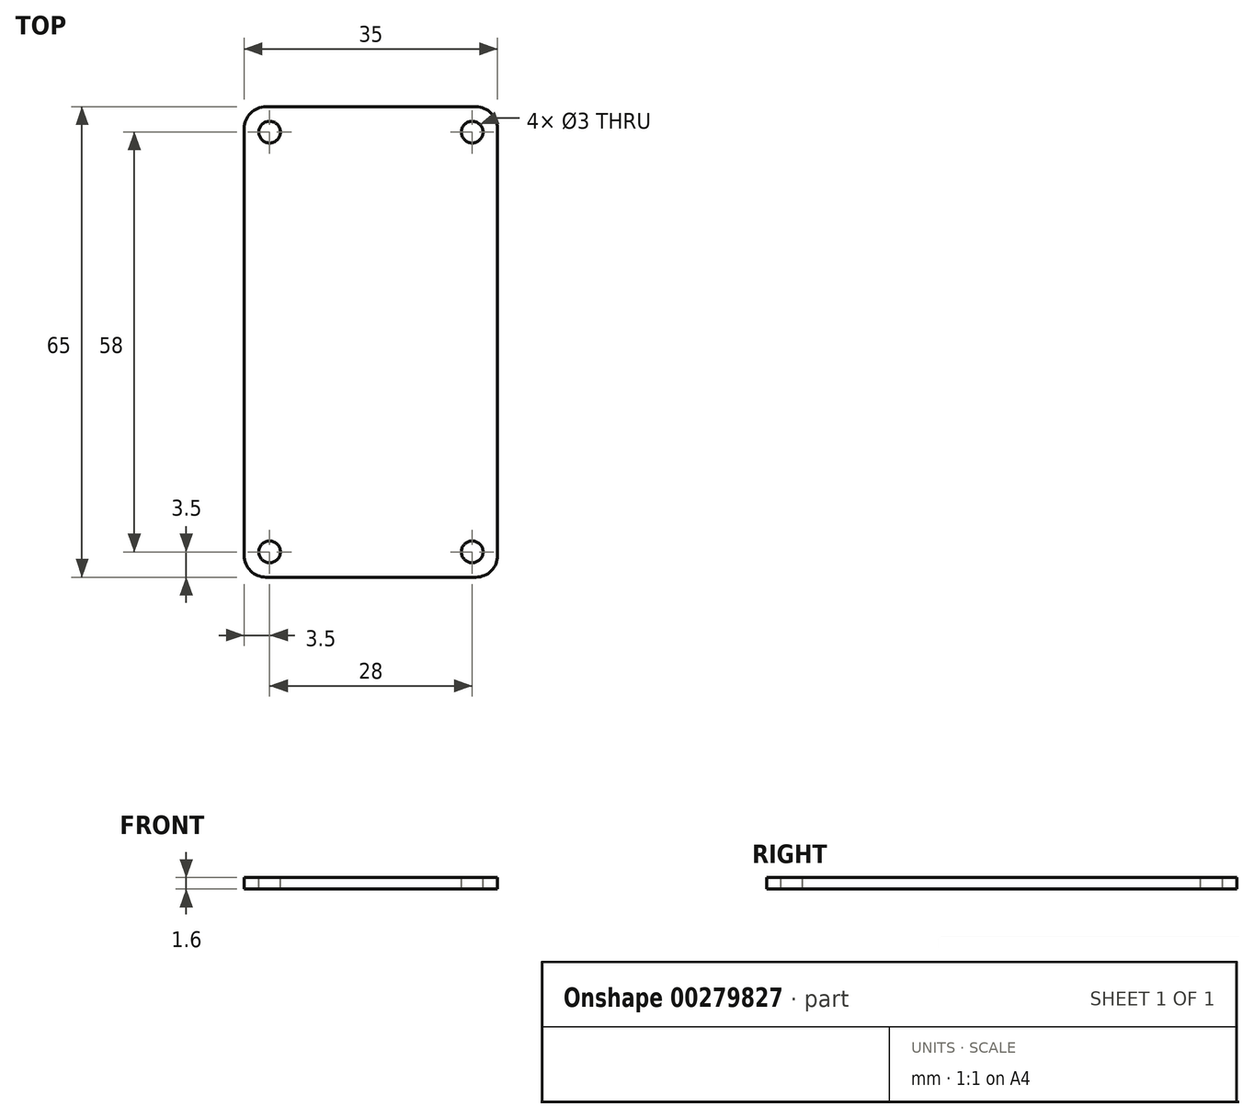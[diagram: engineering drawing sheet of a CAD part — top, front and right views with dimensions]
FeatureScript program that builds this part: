
annotation { "Feature Type Name" : "Feature", "Feature Type Description" : "" }
export const myFeature = defineFeature(function(context is Context, id is Id, definition is map)
    precondition{}
    {
        {
            var Q0;
            Q0=qCreatedBy(makeId("Top.planeOp"),FACE);
            var sketch = newSketch(context, id + "F0", { "sketchPlane" : qUnion([Q0])});
            skLineSegment(sketch, "E0.bottom", {"start": v(14.5, 32.5) * mm, "end": v(-14.5, 32.5) * mm});
            skLineSegment(sketch, "E0.top", {"start": v(14.5, -32.5) * mm, "end": v(-14.5, -32.5) * mm});
            skLineSegment(sketch, "E0.left", {"start": v(17.5, 29.5) * mm, "end": v(17.5, -29.5) * mm});
            skLineSegment(sketch, "E0.right", {"start": v(-17.5, 29.5) * mm, "end": v(-17.5, -29.5) * mm});
            skPoint(sketch, "E0.middle", {"position": v(0, 0) * mm});
            skPoint(sketch, "E1.visualSharp", {"position": v(-17.5, 32.5) * mm});
            skArc(sketch, "E1.filletArc", {"start": v(-14.5, 32.5) * mm, "mid": v(-16.62, 31.62) * mm, "end": v(-17.5, 29.5) * mm});
            skPoint(sketch, "E2.visualSharp", {"position": v(17.5, 32.5) * mm});
            skArc(sketch, "E2.filletArc", {"start": v(17.5, 29.5) * mm, "mid": v(16.62, 31.62) * mm, "end": v(14.5, 32.5) * mm});
            skPoint(sketch, "E3.visualSharp", {"position": v(-17.5, -32.5) * mm});
            skArc(sketch, "E3.filletArc", {"start": v(-17.5, -29.5) * mm, "mid": v(-16.62, -31.62) * mm, "end": v(-14.5, -32.5) * mm});
            skPoint(sketch, "E4.visualSharp", {"position": v(17.5, -32.5) * mm});
            skArc(sketch, "E4.filletArc", {"start": v(14.5, -32.5) * mm, "mid": v(16.62, -31.62) * mm, "end": v(17.5, -29.5) * mm});
            skCircle(sketch, "E5", {"center": v(-14, 29) * mm, "radius": 1.5 * mm});
            skCircle(sketch, "E6", {"center": v(14, 29) * mm, "radius": 1.5 * mm});
            skCircle(sketch, "E7", {"center": v(-14, -29) * mm, "radius": 1.5 * mm});
            skCircle(sketch, "E8", {"center": v(14, -29) * mm, "radius": 1.5 * mm});
            skSolve(sketch);
        }
        {
            var Q0;
            Q0=makeQuery(id+"F0.imprint","IMPRINT",FACE,{"disambiguationData":[TD([[makeQuery(id+"F0.imprint","IMPRINT",EDGE,{"derivedFrom":sQuery(id+"F0.wireOp",EDGE,"E0.bottom")}),1.0]])]});
            extrude(context, id + "F1", {"entities" : qUnion([Q0]), "oppositeDirection" : true, "depth" : 1.6 * mm});
        }
    });
